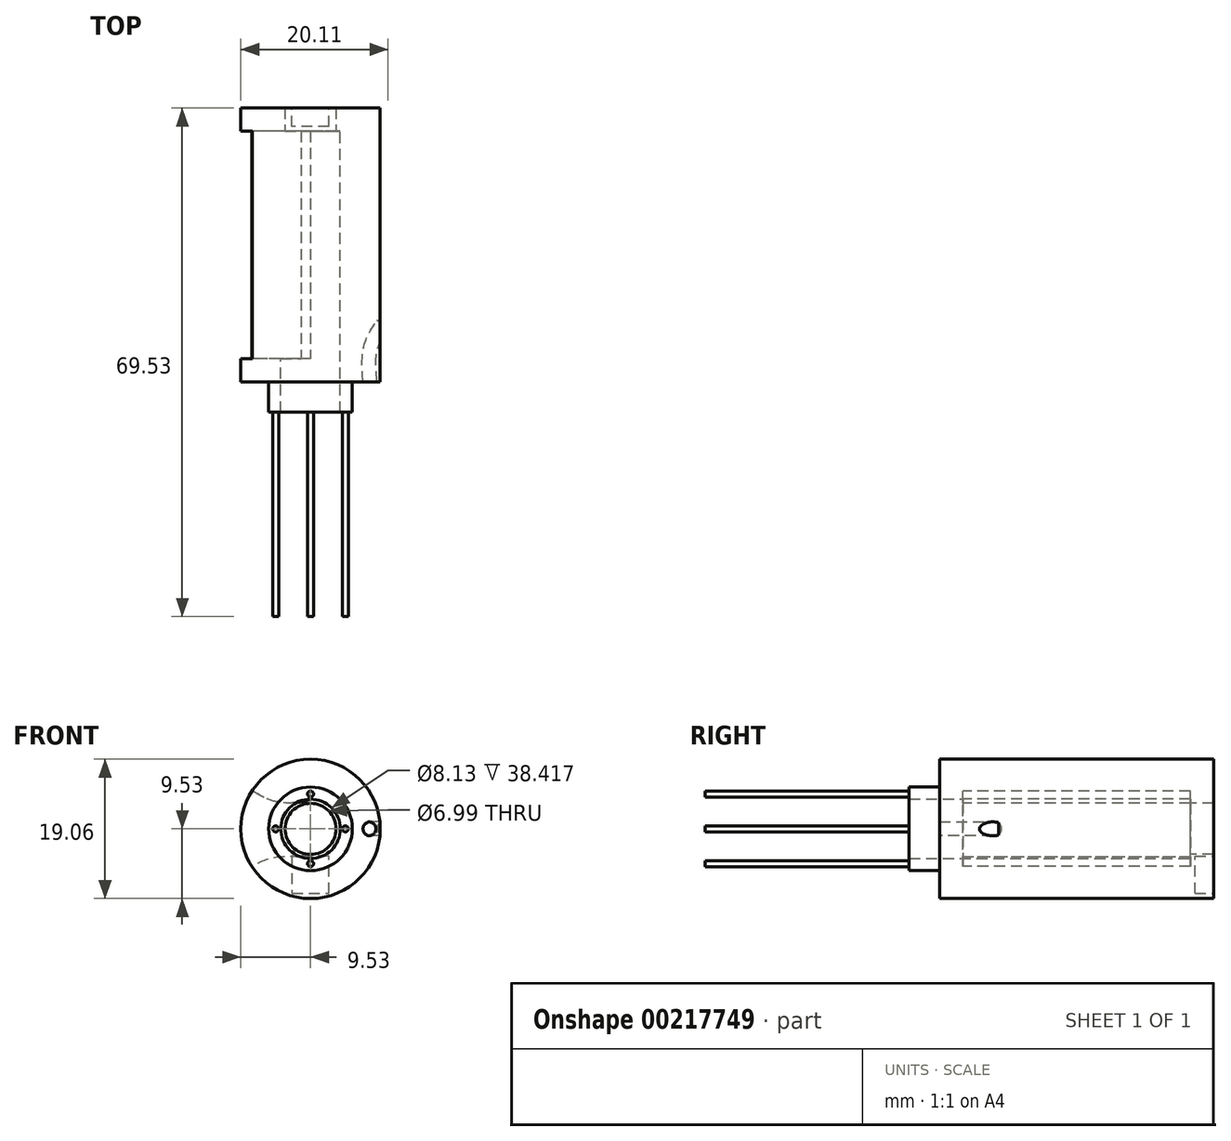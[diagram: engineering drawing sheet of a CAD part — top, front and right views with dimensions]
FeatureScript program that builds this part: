
annotation { "Feature Type Name" : "Feature", "Feature Type Description" : "" }
export const myFeature = defineFeature(function(context is Context, id is Id, definition is map)
    precondition{}
    {
        {
            var Q0;
            Q0=qCreatedBy(makeId("Front.planeOp"),FACE);
            var sketch = newSketch(context, id + "F0", { "sketchPlane" : qUnion([Q0])});
            skCircle(sketch, "E0", {"center": v(0, 0) * mm, "radius": 4.06 * mm});
            skCircle(sketch, "E1", {"center": v(0, 0) * mm, "radius": 5.72 * mm});
            skSolve(sketch);
        }
        {
            var Q0;
            Q0 = qSketchRegion(id + "F0", true);
            extrude(context, id + "F1", {"entities" : qUnion([Q0]), "depth" : 2.54 * mm});
        }
        {
            var Q0;
            Q0=makeQuery(id+"F1.opExtrude","CAP_FACE",FACE,{"disambiguationData":[OSD([sQuery(id+"F0.wireOp",EDGE,"E0"),sQuery(id+"F0.wireOp",EDGE,"E1")])],"isStart":true});
            var sketch = newSketch(context, id + "F2", { "sketchPlane" : qUnion([Q0])});
            skCircle(sketch, "E2", {"center": v(0, 0) * mm, "radius": 5.72 * mm});
            skCircle(sketch, "E3", {"center": v(0, 0) * mm, "radius": 4.06 * mm});
            skSolve(sketch);
        }
        {
            var Q0;
            Q0 = qSketchRegion(id + "F2", true);
            extrude(context, id + "F3", {"entities" : qUnion([Q0]), "operationType" : NewBodyOperationType.ADD, "depth" : 1.59 * mm});
        }
        {
            var Q0;
            Q0=makeQuery(id+"F3.opExtrude","CAP_FACE",FACE,{"disambiguationData":[OSD([sQuery(id+"F2.wireOp",EDGE,"E2"),sQuery(id+"F2.wireOp",EDGE,"E3")])],"isStart":false});
            var sketch = newSketch(context, id + "F4", { "sketchPlane" : qUnion([Q0])});
            skCircle(sketch, "E4", {"center": v(0, 0) * mm, "radius": 9.53 * mm});
            skCircle(sketch, "E5", {"center": v(0, 0) * mm, "radius": 4.06 * mm});
            skSolve(sketch);
        }
        {
            var Q0;
            Q0 = qSketchRegion(id + "F4", true);
            extrude(context, id + "F5", {"entities" : qUnion([Q0]), "operationType" : NewBodyOperationType.ADD, "depth" : 3.17 * mm});
        }
        {
            var Q0;
            Q0=makeQuery(id+"F5.opExtrude","CAP_FACE",FACE,{"disambiguationData":[OSD([sQuery(id+"F4.wireOp",EDGE,"E4"),sQuery(id+"F4.wireOp",EDGE,"E5")])],"isStart":false});
            var sketch = newSketch(context, id + "F6", { "sketchPlane" : qUnion([Q0])});
            skArc(sketch, "E6", {"start": v(8, 5.18) * mm, "mid": v(-9.52, -0.02) * mm, "end": v(8.01, -5.15) * mm});
            skArc(sketch, "E7", {"start": v(0, 4.06) * mm, "mid": v(-4.01, -0.64) * mm, "end": v(1.26, -3.86) * mm});
            skFitSpline(sketch, "E8", {"points": [v(0, 4.06) * mm, v(5.22, 3.84) * mm, v(8, 5.18) * mm], "startDerivative": vector(9.3, -3.6) * mm, "endDerivative": vector(5.88, 3.18) * mm});
            skFitSpline(sketch, "E9.MirrorCS", {"points": [v(0, -3.94) * mm, v(5.22, -4) * mm, v(8.01, -5.15) * mm], "startDerivative": vector(9.96, 0.62) * mm, "endDerivative": vector(5.87, -3.2) * mm});
            skSolve(sketch);
        }
        {
            var Q0;
            Q0 = qSketchRegion(id + "F6", true);
            extrude(context, id + "F7", {"entities" : qUnion([Q0]), "operationType" : NewBodyOperationType.ADD, "depth" : 31.12 * mm});
        }
        {
            var Q0;
            Q0=makeQuery(id+"F7.opExtrude","CAP_FACE",FACE,{"disambiguationData":[OSD([sQuery(id+"F6.wireOp",EDGE,"E6"),sQuery(id+"F6.wireOp",EDGE,"E7"),sQuery(id+"F6.wireOp",EDGE,"E8"),sQuery(id+"F6.wireOp",EDGE,"E9.MirrorCS")])],"isStart":false});
            var sketch = newSketch(context, id + "F8", { "sketchPlane" : qUnion([Q0])});
            skCircle(sketch, "E10", {"center": v(0, 0) * mm, "radius": 3.5 * mm});
            skCircle(sketch, "E11", {"center": v(0, 0) * mm, "radius": 9.53 * mm});
            skSolve(sketch);
        }
        {
            var Q0;
            Q0 = qSketchRegion(id + "F8", true);
            extrude(context, id + "F9", {"entities" : qUnion([Q0]), "operationType" : NewBodyOperationType.ADD, "depth" : 3.17 * mm});
        }
        {
            var Q0;
            Q0=makeQuery(id+"F9.opExtrude","CAP_FACE",FACE,{"disambiguationData":[OSD([sQuery(id+"F8.wireOp",EDGE,"E10"),sQuery(id+"F8.wireOp",EDGE,"E11")])],"isStart":false});
            var sketch = newSketch(context, id + "F10", { "sketchPlane" : qUnion([Q0])});
            skLineSegment(sketch, "E12", {"start": v(2.54, -6.29) * mm, "end": v(2.54, -3.75) * mm});
            skLineSegment(sketch, "E13", {"start": v(-2.54, -6.29) * mm, "end": v(-2.54, -3.75) * mm});
            skLineSegment(sketch, "E14", {"start": v(-2.54, -3.75) * mm, "end": v(2.54, -3.75) * mm});
            skLineSegment(sketch, "E15", {"start": v(2.54, -6.29) * mm, "end": v(2.54, -8.83) * mm});
            skLineSegment(sketch, "E16", {"start": v(2.54, -8.83) * mm, "end": v(-2.54, -8.83) * mm});
            skLineSegment(sketch, "E17", {"start": v(-2.54, -8.83) * mm, "end": v(-2.54, -6.29) * mm});
            skSolve(sketch);
        }
        {
            var Q0;
            Q0 = qSketchRegion(id + "F10", true);
            extrude(context, id + "F11", {"entities" : qUnion([Q0]), "operationType" : NewBodyOperationType.REMOVE, "oppositeDirection" : true, "depth" : 2.54 * mm});
        }
        {
            var Q0;
            Q0=makeQuery(id+"F5.opExtrude","CAP_FACE",FACE,{"disambiguationData":[OSD([sQuery(id+"F4.wireOp",EDGE,"E4"),sQuery(id+"F4.wireOp",EDGE,"E5")])],"isStart":true});
            var sketch = newSketch(context, id + "F12", { "sketchPlane" : qUnion([Q0])});
            skCircle(sketch, "E18", {"center": v(8.12, 0) * mm, "radius": 0.95 * mm});
            skSolve(sketch);
        }
        {
            var Q0;
            Q0=qCreatedBy(makeId("Top.planeOp"),FACE);
            var sketch = newSketch(context, id + "F13", { "sketchPlane" : qUnion([Q0])});
            skFitSpline(sketch, "E19", {"points": [v(8.2, 1.55) * mm, v(8.27, 6.23) * mm, v(9.89, 9.38) * mm], "startDerivative": vector(-0.74, 9.27) * mm, "endDerivative": vector(4.24, 6.3) * mm});
            skSolve(sketch);
        }
        {
            var Q0;
            Q0 = qSketchRegion(id + "F12", true);
            var Q1;
            Q1 = qConstructionFilter(qBodyType(qCreatedBy(id + "F13" ,EDGE), BodyType.WIRE), ConstructionObject.NO);
            sweep(context, id + "F14", {"operationType" : NewBodyOperationType.REMOVE, "profiles" : qUnion([Q0]), "path" : qUnion([Q1])});
        }
        {
            var Q0;
            Q0=makeQuery(id+"F1.opExtrude","CAP_FACE",FACE,{"disambiguationData":[OSD([sQuery(id+"F0.wireOp",EDGE,"E0"),sQuery(id+"F0.wireOp",EDGE,"E1")])],"isStart":false});
            var sketch = newSketch(context, id + "F15", { "sketchPlane" : qUnion([Q0])});
            skCircle(sketch, "E20", {"center": v(4.76, 0) * mm, "radius": 0.41 * mm});
            skPoint(sketch, "E21.center", {"position": v(0, 0) * mm});
            skCircle(sketch, "E22.1.0", {"center": v(0, 4.76) * mm, "radius": 0.41 * mm});
            skCircle(sketch, "E22.2.0", {"center": v(-4.76, 0) * mm, "radius": 0.41 * mm});
            skCircle(sketch, "E22.3.0", {"center": v(0, -4.76) * mm, "radius": 0.41 * mm});
            skSolve(sketch);
        }
        {
            var Q0;
            Q0 = qSketchRegion(id + "F15", true);
            extrude(context, id + "F16", {"entities" : qUnion([Q0]), "operationType" : NewBodyOperationType.ADD, "depth" : 27.94 * mm});
        }
    });
